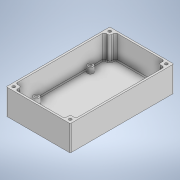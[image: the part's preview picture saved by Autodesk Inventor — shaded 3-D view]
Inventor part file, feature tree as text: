
AUTODESK INVENTOR PART (.ipt)
format: ipt  version: 2021 (Build 250183000, 183)  size: 372,224 bytes
history: native  units: mm
features: fillet x7, extrude x6, sketch x6
ambient origin geometry x8: Origin, YZ Plane, XZ Plane, XY Plane, X Axis, Y Axis, Z Axis, Center Point
bodies: Solid1 (feature_tree)
feature tree (19):
  extrude  "Extrusion1"  Depth=62.0mm
  extrude  "Extrusion2"  Depth=3.0mm
  extrude  "Extrusion3"  Depth=3.0mm
  extrude  "Extrusion4"  Depth=3.0mm
  fillet  "Fillet1"  Radius=6.0mm
  fillet  "Fillet2"  Radius=3.0mm
  fillet  "Fillet3"  Radius=57.4mm
  extrude  "Extrusion5"  Depth=0.8mm
  fillet  "Fillet4"  Radius=51.56mm
  extrude  "Extrusion6"  Depth=6.0mm
  fillet  "Fillet5"  Radius=6.0mm
  fillet  "Fillet6"  Radius=6.0mm
  fillet  "Fillet7"  Radius=20.0mm
  sketch  "Sketch2"  dims[d14=66.0mm d15=62.0mm]
  sketch  "Sketch4"  dims[d16=3.0mm d17=3.0mm]
  sketch  "Sketch5"  dims[d18=3.0mm d19=3.0mm]
  sketch  "Sketch6"  dims[d20=3.0mm d21=4.5mm d22=6.0mm d23=3.0mm d24=57.4mm]
  sketch  "Sketch8"  dims[d25=54.35mm d26=0.8mm d27=51.56mm]
  sketch  "Sketch9"  dims[d28=4.8mm d29=6.0mm d30=6.0mm d31=6.0mm d32=20.0mm d33=20.0mm d34=1.0mm d35=1.0mm d36=2.0mm d37=0.0mm d38=66.0mm d39=62.0mm d40=3.0mm d41=3.0mm d42=3.0mm d43=3.0mm d44=3.0mm d45=4.5mm d46=6.0mm d47=3.0mm d48=57.4mm d49=54.35mm d50=0.8mm d51=51.56mm d52=4.8mm d53=6.0mm d54=6.0mm d55=6.0mm d56=20.0mm d57=20.0mm d58=1.0mm d59=1.0mm d60=0.0mm d61=0.0mm d62=6.0mm d63=0.0mm d64=2.0mm d65=0.0mm d66=2.0mm d67=2.0mm d68=30.0mm d69=4.0mm d70=4.0mm d71=4.0mm d72=2.0mm d73=2.0mm d74=2.0mm d75=2.0mm d76=35.0mm d77=8.0mm d78=0.0mm d79=4.0mm d80=0.0mm d81=1.0mm d82=1.0mm d83=1.0mm d86=2.0mm d87=2.0mm d88=2.0mm d89=2.0mm d90=25.0mm d91=2.0mm d92=0.0mm d93=0.0mm d94=1.0mm d95=3.0mm d96=3.0mm d97=3.0mm d98=3.0mm d99=7.0mm d100=7.0mm d101=7.0mm d102=7.0mm d103=4.0mm d104=4.0mm d105=4.0mm d106=4.0mm d107=4.0mm d108=4.0mm d109=4.0mm d110=4.0mm d111=6.0mm d112=6.0mm d113=6.0mm d114=6.0mm d115=6.0mm d116=6.0mm d117=25.0mm d118=0.0mm d119=2.0mm d120=2.0mm d121=1.0mm]
